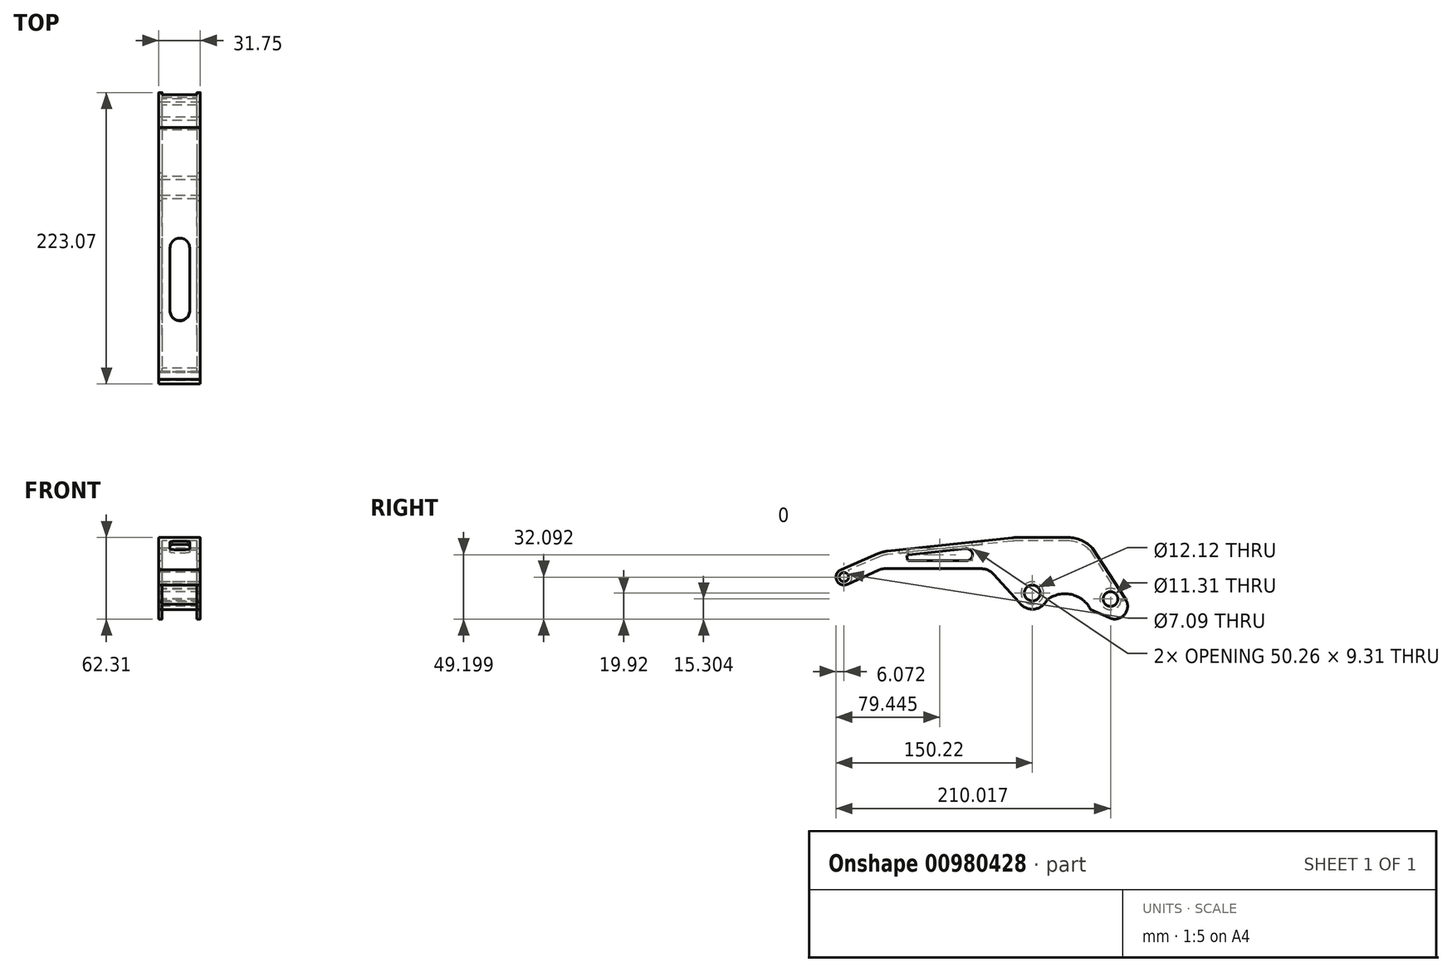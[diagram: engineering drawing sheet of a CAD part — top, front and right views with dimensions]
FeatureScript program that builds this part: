
annotation { "Feature Type Name" : "Feature", "Feature Type Description" : "" }
export const myFeature = defineFeature(function(context is Context, id is Id, definition is map)
    precondition{}
    {
        {
            var Q0;
            Q0=qCreatedBy(makeId("Right.planeOp"),FACE);
            var sketch = newSketch(context, id + "F0", { "sketchPlane" : qUnion([Q0])});
            skCircle(sketch, "E0", {"center": v(0, 0) * mm, "radius": 6.06 * mm});
            skArc(sketch, "E1", {"start": v(-146.46, 17.78) * mm, "mid": v(-149.67, 9.66) * mm, "end": v(-141.44, 6.74) * mm});
            skLineSegment(sketch, "E2", {"start": v(27.36, 42.4) * mm, "end": v(-12.87, 42.4) * mm});
            skLineSegment(sketch, "E3", {"start": v(-15.58, 42.25) * mm, "end": v(-110.86, 32.02) * mm});
            skLineSegment(sketch, "E4", {"start": v(-112.64, 18.6) * mm, "end": v(-39.03, 18.6) * mm});
            skPoint(sketch, "E5.visualSharp", {"position": v(-115.4, 18.6) * mm});
            skArc(sketch, "E5.filletArc", {"start": v(-112.64, 18.6) * mm, "mid": v(-115.33, 18.3) * mm, "end": v(-117.9, 17.46) * mm});
            skPoint(sketch, "E6.visualSharp", {"position": v(-33.39, 18.6) * mm});
            skArc(sketch, "E6.filletArc", {"start": v(-29.6, 14.4) * mm, "mid": v(-33.88, 17.5) * mm, "end": v(-39.03, 18.6) * mm});
            skLineSegment(sketch, "E7", {"start": v(-117.9, 17.46) * mm, "end": v(-141.44, 6.74) * mm});
            skLineSegment(sketch, "E8", {"start": v(-118.3, 30.06) * mm, "end": v(-146.46, 17.78) * mm});
            skPoint(sketch, "E9.visualSharp", {"position": v(-114.73, 31.6) * mm});
            skArc(sketch, "E9.filletArc", {"start": v(-110.86, 32.02) * mm, "mid": v(-114.65, 31.32) * mm, "end": v(-118.3, 30.06) * mm});
            skPoint(sketch, "E10.visualSharp", {"position": v(-14.23, 42.4) * mm});
            skArc(sketch, "E10.filletArc", {"start": v(-12.87, 42.4) * mm, "mid": v(-14.23, 42.36) * mm, "end": v(-15.58, 42.25) * mm});
            skPoint(sketch, "E11.visualSharp", {"position": v(38.52, 42.4) * mm});
            skArc(sketch, "E11.filletArc", {"start": v(46.07, 34.17) * mm, "mid": v(37.58, 40.25) * mm, "end": v(27.36, 42.4) * mm});
            skPoint(sketch, "E12.visualSharp", {"position": v(-4.5, -32.52) * mm});
            skLineSegment(sketch, "E13", {"start": v(46.07, 34.17) * mm, "end": v(71.3, -4.94) * mm});
            skCircle(sketch, "E14", {"center": v(59.8, -4.62) * mm, "radius": 5.65 * mm});
            skLineSegment(sketch, "E15", {"start": v(59.27, -19.12) * mm, "end": v(44.75, -12.82) * mm});
            skArc(sketch, "E16.filletArc", {"start": v(59.27, -19.12) * mm, "mid": v(70.54, -16.5) * mm, "end": v(71.3, -4.94) * mm});
            skCircle(sketch, "E17", {"center": v(-144.15, 12.17) * mm, "radius": 3.55 * mm});
            skArc(sketch, "E18.0", {"start": v(-10.16, -7.12) * mm, "mid": v(1.04, -12.36) * mm, "end": v(11.2, -5.33) * mm});
            skLineSegment(sketch, "E19", {"start": v(-29.6, 14.4) * mm, "end": v(-10.16, -7.12) * mm});
            skArc(sketch, "E20", {"start": v(44.75, -12.82) * mm, "mid": v(29.75, -1.13) * mm, "end": v(11.2, -5.33) * mm});
            skSolve(sketch);
        }
        {
            var Q0;
            Q0 = qSketchRegion(id + "F0", true);
            extrude(context, id + "F1", {"entities" : qUnion([Q0]), "depth" : 31.75 * mm, "offsetDistance" : 25.4 * mm});
        }
        {
            var Q0;
            Q0=makeQuery(id+"F1.opExtrude","SWEPT_FACE",FACE,{"disambiguationData":[OSD([sQuery(id+"F0.wireOp",EDGE,"E7")])]});
            var Q1;
            Q1=makeQuery(id+"F1.opExtrude","SWEPT_FACE",FACE,{"disambiguationData":[OSD([sQuery(id+"F0.wireOp",EDGE,"E5.filletArc")])]});
            var Q2;
            Q2=makeQuery(id+"F1.opExtrude","SWEPT_FACE",FACE,{"disambiguationData":[OSD([sQuery(id+"F0.wireOp",EDGE,"E4")])]});
            var Q3;
            Q3=makeQuery(id+"F1.opExtrude","SWEPT_FACE",FACE,{"disambiguationData":[OSD([sQuery(id+"F0.wireOp",EDGE,"E6.filletArc")])]});
            var Q4;
            Q4=makeQuery(id+"F1.opExtrude","SWEPT_FACE",FACE,{"disambiguationData":[OSD([sQuery(id+"F0.wireOp",EDGE,"E19")])]});
            var Q5;
            Q5=makeQuery(id+"F1.opExtrude","SWEPT_FACE",FACE,{"disambiguationData":[OSD([sQuery(id+"F0.wireOp",EDGE,"E18.0")])]});
            var Q6;
            Q6=makeQuery(id+"F1.opExtrude","SWEPT_FACE",FACE,{"disambiguationData":[OSD([sQuery(id+"F0.wireOp",EDGE,"E20")])]});
            var Q7;
            Q7=makeQuery(id+"F1.opExtrude","SWEPT_FACE",FACE,{"disambiguationData":[OSD([sQuery(id+"F0.wireOp",EDGE,"E15")])]});
            var Q8;
            Q8=makeQuery(id+"F1.opExtrude","SWEPT_FACE",FACE,{"disambiguationData":[OSD([sQuery(id+"F0.wireOp",EDGE,"E16.filletArc")])]});
            shell(context, id + "F2", {"entities" : qUnion([Q0, Q1, Q2, Q3, Q4, Q5, Q6, Q7, Q8]), "thickness" : 2.54 * mm});
        }
        {
            var Q0;
            Q0=makeQuery(id+"F1.opExtrude","SWEPT_FACE",FACE,{"disambiguationData":[OSD([sQuery(id+"F0.wireOp",EDGE,"E3")])]});
            var sketch = newSketch(context, id + "F3", { "sketchPlane" : qUnion([Q0])});
            skArc(sketch, "E21", {"start": v(8.59, -90.62) * mm, "mid": v(15.99, -97.73) * mm, "end": v(23.53, -90.78) * mm});
            skArc(sketch, "E22", {"start": v(23.53, -42.08) * mm, "mid": v(16.33, -34.07) * mm, "end": v(8.58, -41.55) * mm});
            skLineSegment(sketch, "E23", {"start": v(8.59, -90.62) * mm, "end": v(8.58, -41.55) * mm});
            skLineSegment(sketch, "E24", {"start": v(23.53, -90.78) * mm, "end": v(23.53, -42.08) * mm});
            skSolve(sketch);
        }
        {
            var Q0;
            Q0 = qSketchRegion(id + "F3", true);
            extrude(context, id + "F4", {"entities" : qUnion([Q0]), "operationType" : NewBodyOperationType.REMOVE, "oppositeDirection" : true, "depth" : 25.4 * mm, "offsetDistance" : 25.4 * mm});
        }
        {
            var Q0;
            Q0=makeQuery(id+"F1.opExtrude","CAP_FACE",FACE,{"disambiguationData":[OSD([sQuery(id+"F0.wireOp",EDGE,"E0"),sQuery(id+"F0.wireOp",EDGE,"E1"),sQuery(id+"F0.wireOp",EDGE,"E2"),sQuery(id+"F0.wireOp",EDGE,"E3"),sQuery(id+"F0.wireOp",EDGE,"E4"),sQuery(id+"F0.wireOp",EDGE,"E5.filletArc"),sQuery(id+"F0.wireOp",EDGE,"E6.filletArc"),sQuery(id+"F0.wireOp",EDGE,"E7"),sQuery(id+"F0.wireOp",EDGE,"E8"),sQuery(id+"F0.wireOp",EDGE,"E9.filletArc"),sQuery(id+"F0.wireOp",EDGE,"E10.filletArc"),sQuery(id+"F0.wireOp",EDGE,"E11.filletArc"),sQuery(id+"F0.wireOp",EDGE,"E13"),sQuery(id+"F0.wireOp",EDGE,"E14"),sQuery(id+"F0.wireOp",EDGE,"E15"),sQuery(id+"F0.wireOp",EDGE,"E16.filletArc"),sQuery(id+"F0.wireOp",EDGE,"E17"),sQuery(id+"F0.wireOp",EDGE,"E18.0"),sQuery(id+"F0.wireOp",EDGE,"E19"),sQuery(id+"F0.wireOp",EDGE,"E20")])],"isStart":false});
            var sketch = newSketch(context, id + "F5", { "sketchPlane" : qUnion([Q0])});
            skLineSegment(sketch, "E25", {"start": v(-96.05, 29.1) * mm, "end": v(-46.13, 34.46) * mm});
            skLineSegment(sketch, "E26", {"start": v(-46.13, 34.46) * mm, "end": v(-45.07, 24.63) * mm});
            skLineSegment(sketch, "E27", {"start": v(-45.07, 24.63) * mm, "end": v(-95.51, 24.63) * mm});
            skLineSegment(sketch, "E28", {"start": v(-95.51, 24.63) * mm, "end": v(-96.05, 29.1) * mm});
            skSolve(sketch);
        }
        {
            var Q0;
            Q0 = qSketchRegion(id + "F5", true);
            extrude(context, id + "F6", {"entities" : qUnion([Q0]), "operationType" : NewBodyOperationType.REMOVE, "endBound" : BoundingType.THROUGH_ALL, "oppositeDirection" : true, "depth" : 25.4 * mm, "offsetDistance" : 25.4 * mm});
        }
        {
            var Q0;
            {var subQ0=sQuery(id+"F0.wireOp",EDGE,"E20");var subQ1=sQuery(id+"F0.wireOp",EDGE,"E19");var subQ2=sQuery(id+"F0.wireOp",EDGE,"E18.0");var subQ3=sQuery(id+"F0.wireOp",EDGE,"E17");var subQ4=sQuery(id+"F0.wireOp",EDGE,"E16.filletArc");var subQ5=sQuery(id+"F0.wireOp",EDGE,"E15");var subQ6=sQuery(id+"F0.wireOp",EDGE,"E14");var subQ7=sQuery(id+"F0.wireOp",EDGE,"E13");var subQ8=sQuery(id+"F0.wireOp",EDGE,"E11.filletArc");var subQ9=sQuery(id+"F0.wireOp",EDGE,"E10.filletArc");var subQ10=sQuery(id+"F0.wireOp",EDGE,"E9.filletArc");var subQ11=sQuery(id+"F0.wireOp",EDGE,"E8");var subQ12=sQuery(id+"F0.wireOp",EDGE,"E7");var subQ13=sQuery(id+"F0.wireOp",EDGE,"E6.filletArc");var subQ14=sQuery(id+"F0.wireOp",EDGE,"E5.filletArc");var subQ15=sQuery(id+"F0.wireOp",EDGE,"E4");var subQ16=sQuery(id+"F0.wireOp",EDGE,"E3");var subQ17=sQuery(id+"F0.wireOp",EDGE,"E2");var subQ18=sQuery(id+"F0.wireOp",EDGE,"E1");var subQ19=sQuery(id+"F0.wireOp",EDGE,"E0");var subQ20=makeQuery(id+"F1.opExtrude","CAP_FACE",FACE,{"disambiguationData":[OSD([subQ19,subQ18,subQ17,subQ16,subQ15,subQ14,subQ13,subQ12,subQ11,subQ10,subQ9,subQ8,subQ7,subQ6,subQ5,subQ4,subQ3,subQ2,subQ1,subQ0])],"isStart":false});var subQ21=sQuery(id+"F5.wireOp",EDGE,"E27");var subQ22=sQuery(id+"F5.wireOp",EDGE,"E26");Q0=makeQuery(id+"F6.boolean.opBoolean","COPY",EDGE,{"disambiguationData":[TD([subQ20])],"derivedFrom":makeQuery(id+"F6.opExtrude","SWEPT_EDGE",EDGE,{"disambiguationData":[OSD([subQ22,subQ21])]})});}
            var Q1;
            {var subQ0=sQuery(id+"F0.wireOp",EDGE,"E20");var subQ1=sQuery(id+"F0.wireOp",EDGE,"E19");var subQ2=sQuery(id+"F0.wireOp",EDGE,"E18.0");var subQ3=sQuery(id+"F0.wireOp",EDGE,"E17");var subQ4=sQuery(id+"F0.wireOp",EDGE,"E16.filletArc");var subQ5=sQuery(id+"F0.wireOp",EDGE,"E15");var subQ6=sQuery(id+"F0.wireOp",EDGE,"E14");var subQ7=sQuery(id+"F0.wireOp",EDGE,"E13");var subQ8=sQuery(id+"F0.wireOp",EDGE,"E11.filletArc");var subQ9=sQuery(id+"F0.wireOp",EDGE,"E10.filletArc");var subQ10=sQuery(id+"F0.wireOp",EDGE,"E9.filletArc");var subQ11=sQuery(id+"F0.wireOp",EDGE,"E8");var subQ12=sQuery(id+"F0.wireOp",EDGE,"E7");var subQ13=sQuery(id+"F0.wireOp",EDGE,"E6.filletArc");var subQ14=sQuery(id+"F0.wireOp",EDGE,"E5.filletArc");var subQ15=sQuery(id+"F0.wireOp",EDGE,"E4");var subQ16=sQuery(id+"F0.wireOp",EDGE,"E3");var subQ17=sQuery(id+"F0.wireOp",EDGE,"E2");var subQ18=sQuery(id+"F0.wireOp",EDGE,"E1");var subQ19=sQuery(id+"F0.wireOp",EDGE,"E0");var subQ20=makeQuery(id+"F1.opExtrude","CAP_FACE",FACE,{"disambiguationData":[OSD([subQ19,subQ18,subQ17,subQ16,subQ15,subQ14,subQ13,subQ12,subQ11,subQ10,subQ9,subQ8,subQ7,subQ6,subQ5,subQ4,subQ3,subQ2,subQ1,subQ0])],"isStart":false});var subQ21=sQuery(id+"F5.wireOp",EDGE,"E25");var subQ22=sQuery(id+"F5.wireOp",EDGE,"E26");Q1=makeQuery(id+"F6.boolean.opBoolean","COPY",EDGE,{"disambiguationData":[TD([subQ20])],"derivedFrom":makeQuery(id+"F6.opExtrude","SWEPT_EDGE",EDGE,{"disambiguationData":[OSD([subQ21,subQ22])]})});}
            var Q2;
            {var subQ0=sQuery(id+"F0.wireOp",EDGE,"E20");var subQ1=sQuery(id+"F0.wireOp",EDGE,"E19");var subQ2=sQuery(id+"F0.wireOp",EDGE,"E18.0");var subQ3=sQuery(id+"F0.wireOp",EDGE,"E17");var subQ4=sQuery(id+"F0.wireOp",EDGE,"E16.filletArc");var subQ5=sQuery(id+"F0.wireOp",EDGE,"E15");var subQ6=sQuery(id+"F0.wireOp",EDGE,"E14");var subQ7=sQuery(id+"F0.wireOp",EDGE,"E13");var subQ8=sQuery(id+"F0.wireOp",EDGE,"E11.filletArc");var subQ9=sQuery(id+"F0.wireOp",EDGE,"E10.filletArc");var subQ10=sQuery(id+"F0.wireOp",EDGE,"E9.filletArc");var subQ11=sQuery(id+"F0.wireOp",EDGE,"E8");var subQ12=sQuery(id+"F0.wireOp",EDGE,"E7");var subQ13=sQuery(id+"F0.wireOp",EDGE,"E6.filletArc");var subQ14=sQuery(id+"F0.wireOp",EDGE,"E5.filletArc");var subQ15=sQuery(id+"F0.wireOp",EDGE,"E4");var subQ16=sQuery(id+"F0.wireOp",EDGE,"E3");var subQ17=sQuery(id+"F0.wireOp",EDGE,"E2");var subQ18=sQuery(id+"F0.wireOp",EDGE,"E1");var subQ19=sQuery(id+"F0.wireOp",EDGE,"E0");var subQ20=makeQuery(id+"F1.opExtrude","CAP_FACE",FACE,{"disambiguationData":[OSD([subQ19,subQ18,subQ17,subQ16,subQ15,subQ14,subQ13,subQ12,subQ11,subQ10,subQ9,subQ8,subQ7,subQ6,subQ5,subQ4,subQ3,subQ2,subQ1,subQ0])],"isStart":true});var subQ21=sQuery(id+"F5.wireOp",EDGE,"E26");var subQ22=sQuery(id+"F5.wireOp",EDGE,"E25");Q2=makeQuery(id+"F6.boolean.opBoolean","COPY",EDGE,{"disambiguationData":[TD([subQ20])],"derivedFrom":makeQuery(id+"F6.opExtrude","SWEPT_EDGE",EDGE,{"disambiguationData":[OSD([subQ22,subQ21])]})});}
            var Q3;
            {var subQ0=sQuery(id+"F0.wireOp",EDGE,"E20");var subQ1=sQuery(id+"F0.wireOp",EDGE,"E19");var subQ2=sQuery(id+"F0.wireOp",EDGE,"E18.0");var subQ3=sQuery(id+"F0.wireOp",EDGE,"E17");var subQ4=sQuery(id+"F0.wireOp",EDGE,"E16.filletArc");var subQ5=sQuery(id+"F0.wireOp",EDGE,"E15");var subQ6=sQuery(id+"F0.wireOp",EDGE,"E14");var subQ7=sQuery(id+"F0.wireOp",EDGE,"E13");var subQ8=sQuery(id+"F0.wireOp",EDGE,"E11.filletArc");var subQ9=sQuery(id+"F0.wireOp",EDGE,"E10.filletArc");var subQ10=sQuery(id+"F0.wireOp",EDGE,"E9.filletArc");var subQ11=sQuery(id+"F0.wireOp",EDGE,"E8");var subQ12=sQuery(id+"F0.wireOp",EDGE,"E7");var subQ13=sQuery(id+"F0.wireOp",EDGE,"E6.filletArc");var subQ14=sQuery(id+"F0.wireOp",EDGE,"E5.filletArc");var subQ15=sQuery(id+"F0.wireOp",EDGE,"E4");var subQ16=sQuery(id+"F0.wireOp",EDGE,"E3");var subQ17=sQuery(id+"F0.wireOp",EDGE,"E2");var subQ18=sQuery(id+"F0.wireOp",EDGE,"E1");var subQ19=sQuery(id+"F0.wireOp",EDGE,"E0");var subQ20=makeQuery(id+"F1.opExtrude","CAP_FACE",FACE,{"disambiguationData":[OSD([subQ19,subQ18,subQ17,subQ16,subQ15,subQ14,subQ13,subQ12,subQ11,subQ10,subQ9,subQ8,subQ7,subQ6,subQ5,subQ4,subQ3,subQ2,subQ1,subQ0])],"isStart":true});var subQ21=sQuery(id+"F5.wireOp",EDGE,"E26");var subQ22=sQuery(id+"F5.wireOp",EDGE,"E27");Q3=makeQuery(id+"F6.boolean.opBoolean","COPY",EDGE,{"disambiguationData":[TD([subQ20])],"derivedFrom":makeQuery(id+"F6.opExtrude","SWEPT_EDGE",EDGE,{"disambiguationData":[OSD([subQ21,subQ22])]})});}
            fillet(context, id + "F7", {"entities" : qUnion([Q0, Q1, Q2, Q3]), "radius" : 5.08 * mm, "tangentPropagation" : true, "allowEdgeOverflow" : false});
        }
        {
            var Q0;
            {var subQ0=sQuery(id+"F0.wireOp",EDGE,"E20");var subQ1=sQuery(id+"F0.wireOp",EDGE,"E19");var subQ2=sQuery(id+"F0.wireOp",EDGE,"E18.0");var subQ3=sQuery(id+"F0.wireOp",EDGE,"E17");var subQ4=sQuery(id+"F0.wireOp",EDGE,"E16.filletArc");var subQ5=sQuery(id+"F0.wireOp",EDGE,"E15");var subQ6=sQuery(id+"F0.wireOp",EDGE,"E14");var subQ7=sQuery(id+"F0.wireOp",EDGE,"E13");var subQ8=sQuery(id+"F0.wireOp",EDGE,"E11.filletArc");var subQ9=sQuery(id+"F0.wireOp",EDGE,"E10.filletArc");var subQ10=sQuery(id+"F0.wireOp",EDGE,"E9.filletArc");var subQ11=sQuery(id+"F0.wireOp",EDGE,"E8");var subQ12=sQuery(id+"F0.wireOp",EDGE,"E7");var subQ13=sQuery(id+"F0.wireOp",EDGE,"E6.filletArc");var subQ14=sQuery(id+"F0.wireOp",EDGE,"E5.filletArc");var subQ15=sQuery(id+"F0.wireOp",EDGE,"E4");var subQ16=sQuery(id+"F0.wireOp",EDGE,"E3");var subQ17=sQuery(id+"F0.wireOp",EDGE,"E2");var subQ18=sQuery(id+"F0.wireOp",EDGE,"E1");var subQ19=sQuery(id+"F0.wireOp",EDGE,"E0");var subQ20=makeQuery(id+"F1.opExtrude","CAP_FACE",FACE,{"disambiguationData":[OSD([subQ19,subQ18,subQ17,subQ16,subQ15,subQ14,subQ13,subQ12,subQ11,subQ10,subQ9,subQ8,subQ7,subQ6,subQ5,subQ4,subQ3,subQ2,subQ1,subQ0])],"isStart":false});var subQ21=sQuery(id+"F5.wireOp",EDGE,"E25");var subQ22=sQuery(id+"F5.wireOp",EDGE,"E28");Q0=makeQuery(id+"F6.boolean.opBoolean","COPY",EDGE,{"disambiguationData":[TD([subQ20])],"derivedFrom":makeQuery(id+"F6.opExtrude","SWEPT_EDGE",EDGE,{"disambiguationData":[OSD([subQ21,subQ22])]})});}
            var Q1;
            {var subQ0=sQuery(id+"F0.wireOp",EDGE,"E20");var subQ1=sQuery(id+"F0.wireOp",EDGE,"E19");var subQ2=sQuery(id+"F0.wireOp",EDGE,"E18.0");var subQ3=sQuery(id+"F0.wireOp",EDGE,"E17");var subQ4=sQuery(id+"F0.wireOp",EDGE,"E16.filletArc");var subQ5=sQuery(id+"F0.wireOp",EDGE,"E15");var subQ6=sQuery(id+"F0.wireOp",EDGE,"E14");var subQ7=sQuery(id+"F0.wireOp",EDGE,"E13");var subQ8=sQuery(id+"F0.wireOp",EDGE,"E11.filletArc");var subQ9=sQuery(id+"F0.wireOp",EDGE,"E10.filletArc");var subQ10=sQuery(id+"F0.wireOp",EDGE,"E9.filletArc");var subQ11=sQuery(id+"F0.wireOp",EDGE,"E8");var subQ12=sQuery(id+"F0.wireOp",EDGE,"E7");var subQ13=sQuery(id+"F0.wireOp",EDGE,"E6.filletArc");var subQ14=sQuery(id+"F0.wireOp",EDGE,"E5.filletArc");var subQ15=sQuery(id+"F0.wireOp",EDGE,"E4");var subQ16=sQuery(id+"F0.wireOp",EDGE,"E3");var subQ17=sQuery(id+"F0.wireOp",EDGE,"E2");var subQ18=sQuery(id+"F0.wireOp",EDGE,"E1");var subQ19=sQuery(id+"F0.wireOp",EDGE,"E0");var subQ20=makeQuery(id+"F1.opExtrude","CAP_FACE",FACE,{"disambiguationData":[OSD([subQ19,subQ18,subQ17,subQ16,subQ15,subQ14,subQ13,subQ12,subQ11,subQ10,subQ9,subQ8,subQ7,subQ6,subQ5,subQ4,subQ3,subQ2,subQ1,subQ0])],"isStart":false});var subQ21=sQuery(id+"F5.wireOp",EDGE,"E27");var subQ22=sQuery(id+"F5.wireOp",EDGE,"E28");Q1=makeQuery(id+"F6.boolean.opBoolean","COPY",EDGE,{"disambiguationData":[TD([subQ20])],"derivedFrom":makeQuery(id+"F6.opExtrude","SWEPT_EDGE",EDGE,{"disambiguationData":[OSD([subQ21,subQ22])]})});}
            var Q2;
            {var subQ0=sQuery(id+"F0.wireOp",EDGE,"E20");var subQ1=sQuery(id+"F0.wireOp",EDGE,"E19");var subQ2=sQuery(id+"F0.wireOp",EDGE,"E18.0");var subQ3=sQuery(id+"F0.wireOp",EDGE,"E17");var subQ4=sQuery(id+"F0.wireOp",EDGE,"E16.filletArc");var subQ5=sQuery(id+"F0.wireOp",EDGE,"E15");var subQ6=sQuery(id+"F0.wireOp",EDGE,"E14");var subQ7=sQuery(id+"F0.wireOp",EDGE,"E13");var subQ8=sQuery(id+"F0.wireOp",EDGE,"E11.filletArc");var subQ9=sQuery(id+"F0.wireOp",EDGE,"E10.filletArc");var subQ10=sQuery(id+"F0.wireOp",EDGE,"E9.filletArc");var subQ11=sQuery(id+"F0.wireOp",EDGE,"E8");var subQ12=sQuery(id+"F0.wireOp",EDGE,"E7");var subQ13=sQuery(id+"F0.wireOp",EDGE,"E6.filletArc");var subQ14=sQuery(id+"F0.wireOp",EDGE,"E5.filletArc");var subQ15=sQuery(id+"F0.wireOp",EDGE,"E4");var subQ16=sQuery(id+"F0.wireOp",EDGE,"E3");var subQ17=sQuery(id+"F0.wireOp",EDGE,"E2");var subQ18=sQuery(id+"F0.wireOp",EDGE,"E1");var subQ19=sQuery(id+"F0.wireOp",EDGE,"E0");var subQ20=makeQuery(id+"F1.opExtrude","CAP_FACE",FACE,{"disambiguationData":[OSD([subQ19,subQ18,subQ17,subQ16,subQ15,subQ14,subQ13,subQ12,subQ11,subQ10,subQ9,subQ8,subQ7,subQ6,subQ5,subQ4,subQ3,subQ2,subQ1,subQ0])],"isStart":true});var subQ21=sQuery(id+"F5.wireOp",EDGE,"E25");var subQ22=sQuery(id+"F5.wireOp",EDGE,"E28");Q2=makeQuery(id+"F6.boolean.opBoolean","COPY",EDGE,{"disambiguationData":[TD([subQ20])],"derivedFrom":makeQuery(id+"F6.opExtrude","SWEPT_EDGE",EDGE,{"disambiguationData":[OSD([subQ21,subQ22])]})});}
            var Q3;
            {var subQ0=sQuery(id+"F0.wireOp",EDGE,"E20");var subQ1=sQuery(id+"F0.wireOp",EDGE,"E19");var subQ2=sQuery(id+"F0.wireOp",EDGE,"E18.0");var subQ3=sQuery(id+"F0.wireOp",EDGE,"E17");var subQ4=sQuery(id+"F0.wireOp",EDGE,"E16.filletArc");var subQ5=sQuery(id+"F0.wireOp",EDGE,"E15");var subQ6=sQuery(id+"F0.wireOp",EDGE,"E14");var subQ7=sQuery(id+"F0.wireOp",EDGE,"E13");var subQ8=sQuery(id+"F0.wireOp",EDGE,"E11.filletArc");var subQ9=sQuery(id+"F0.wireOp",EDGE,"E10.filletArc");var subQ10=sQuery(id+"F0.wireOp",EDGE,"E9.filletArc");var subQ11=sQuery(id+"F0.wireOp",EDGE,"E8");var subQ12=sQuery(id+"F0.wireOp",EDGE,"E7");var subQ13=sQuery(id+"F0.wireOp",EDGE,"E6.filletArc");var subQ14=sQuery(id+"F0.wireOp",EDGE,"E5.filletArc");var subQ15=sQuery(id+"F0.wireOp",EDGE,"E4");var subQ16=sQuery(id+"F0.wireOp",EDGE,"E3");var subQ17=sQuery(id+"F0.wireOp",EDGE,"E2");var subQ18=sQuery(id+"F0.wireOp",EDGE,"E1");var subQ19=sQuery(id+"F0.wireOp",EDGE,"E0");var subQ20=makeQuery(id+"F1.opExtrude","CAP_FACE",FACE,{"disambiguationData":[OSD([subQ19,subQ18,subQ17,subQ16,subQ15,subQ14,subQ13,subQ12,subQ11,subQ10,subQ9,subQ8,subQ7,subQ6,subQ5,subQ4,subQ3,subQ2,subQ1,subQ0])],"isStart":true});var subQ21=sQuery(id+"F5.wireOp",EDGE,"E28");var subQ22=sQuery(id+"F5.wireOp",EDGE,"E27");Q3=makeQuery(id+"F6.boolean.opBoolean","COPY",EDGE,{"disambiguationData":[TD([subQ20])],"derivedFrom":makeQuery(id+"F6.opExtrude","SWEPT_EDGE",EDGE,{"disambiguationData":[OSD([subQ22,subQ21])]})});}
            fillet(context, id + "F8", {"entities" : qUnion([Q0, Q1, Q2, Q3]), "radius" : 1.27 * mm, "tangentPropagation" : true, "allowEdgeOverflow" : false});
        }
    });
